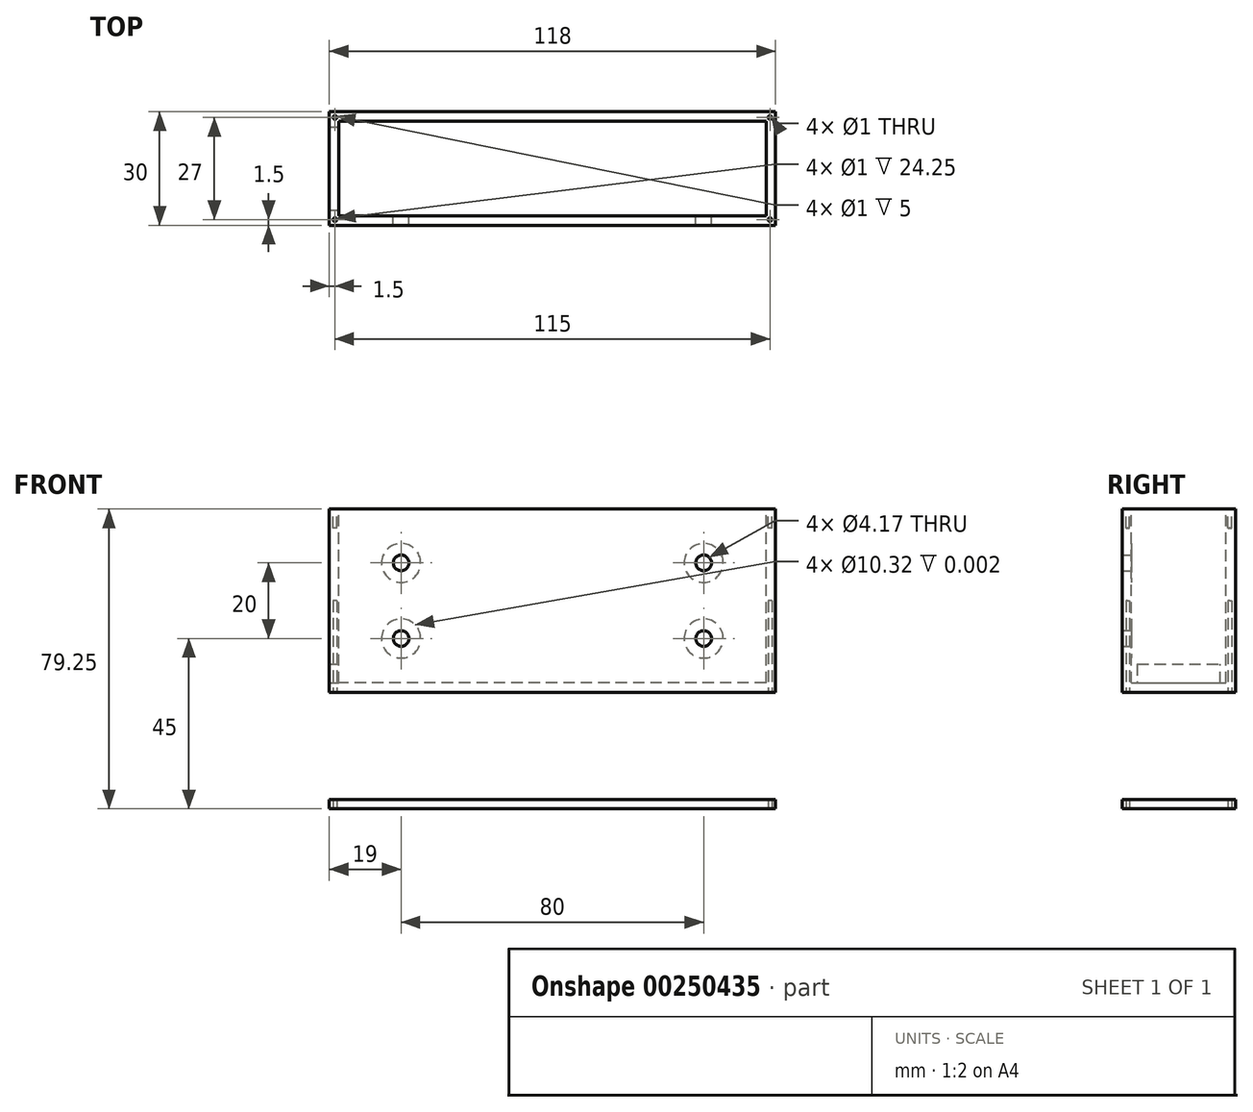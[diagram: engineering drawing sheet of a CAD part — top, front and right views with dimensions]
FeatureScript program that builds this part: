
annotation { "Feature Type Name" : "Feature", "Feature Type Description" : "" }
export const myFeature = defineFeature(function(context is Context, id is Id, definition is map)
    precondition{}
    {
        {
            var Q0;
            Q0=qCreatedBy(makeId("Front.planeOp"),FACE);
            var sketch = newSketch(context, id + "F0", { "sketchPlane" : qUnion([Q0])});
            skLineSegment(sketch, "E0.bottom", {"start": v(59, -24.25) * mm, "end": v(-59, -24.25) * mm});
            skLineSegment(sketch, "E0.top", {"start": v(59, 24.25) * mm, "end": v(-59, 24.25) * mm});
            skLineSegment(sketch, "E0.left", {"start": v(59, -24.25) * mm, "end": v(59, 24.25) * mm});
            skLineSegment(sketch, "E0.right", {"start": v(-59, -24.25) * mm, "end": v(-59, 24.25) * mm});
            skPoint(sketch, "E0.middle", {"position": v(0, 0) * mm});
            skSolve(sketch);
        }
        {
            var Q0;
            Q0 = qSketchRegion(id + "F0", true);
            extrude(context, id + "F1", {"entities" : qUnion([Q0]), "endBound" : BoundingType.SYMMETRIC, "depth" : 30 * mm});
        }
        {
            var Q0;
            Q0=makeQuery(id+"F1.opExtrude","SWEPT_FACE",FACE,{"disambiguationData":[OSD([sQuery(id+"F0.wireOp",EDGE,"E0.top")])]});
            shell(context, id + "F2", {"entities" : qUnion([Q0]), "thickness" : 2.5 * mm});
        }
        {
            var Q0;
            Q0=qCreatedBy(makeId("Right.planeOp"),FACE);
            var sketch = newSketch(context, id + "F3", { "sketchPlane" : qUnion([Q0])});
            skLineSegment(sketch, "E1", {"start": v(11, -16.75) * mm, "end": v(11, -21.75) * mm});
            skLineSegment(sketch, "E2", {"start": v(11, -21.75) * mm, "end": v(-11, -21.75) * mm});
            skLineSegment(sketch, "E3", {"start": v(-11, -21.75) * mm, "end": v(-11, -16.75) * mm});
            skLineSegment(sketch, "E4", {"start": v(11, -16.75) * mm, "end": v(-11, -16.75) * mm});
            skSolve(sketch);
        }
        {
            var Q0;
            Q0 = qSketchRegion(id + "F3", true);
            extrude(context, id + "F4", {"entities" : qUnion([Q0]), "operationType" : NewBodyOperationType.REMOVE, "oppositeDirection" : true, "depth" : 59.4 * mm});
        }
        {
            var Q0;
            Q0=qCreatedBy(makeId("Front.planeOp"),FACE);
            var sketch = newSketch(context, id + "F5", { "sketchPlane" : qUnion([Q0])});
            skCircle(sketch, "E5", {"center": v(40, -10) * mm, "radius": 2.08 * mm});
            skPoint(sketch, "E5.first.point", {"position": v(41.68, -8.77) * mm});
            skPoint(sketch, "E5.second.point", {"position": v(38.45, -11.4) * mm});
            skPoint(sketch, "E5.third.point", {"position": v(38.25, -8.87) * mm});
            skCircle(sketch, "E6", {"center": v(-40, -10) * mm, "radius": 2.08 * mm});
            skCircle(sketch, "E7", {"center": v(-40, 10) * mm, "radius": 2.08 * mm});
            skCircle(sketch, "E8", {"center": v(40, 10) * mm, "radius": 2.08 * mm});
            skSolve(sketch);
        }
        {
            var Q0;
            Q0 = qSketchRegion(id + "F5", true);
            extrude(context, id + "F6", {"entities" : qUnion([Q0]), "operationType" : NewBodyOperationType.REMOVE, "depth" : 25 * mm});
        }
        {
            var Q0;
            Q0=qCreatedBy(makeId("Top.planeOp"),FACE);
            cPlane(context, id + "F7", {"entities" : qUnion([Q0]), "cplaneType" : CPlaneType.OFFSET, "offset" : 55 * mm, "oppositeDirection" : true, "width" : 150 * mm, "height" : 150 * mm});
        }
        {
            var Q0;
            Q0=qCreatedBy(id+"F7.planeOp",FACE);
            var sketch = newSketch(context, id + "F8", { "sketchPlane" : qUnion([Q0])});
            skLineSegment(sketch, "E9.bottom", {"start": v(59, -15) * mm, "end": v(-59, -15) * mm});
            skLineSegment(sketch, "E9.top", {"start": v(59, 15) * mm, "end": v(-59, 15) * mm});
            skLineSegment(sketch, "E9.left", {"start": v(59, -15) * mm, "end": v(59, 15) * mm});
            skLineSegment(sketch, "E9.right", {"start": v(-59, -15) * mm, "end": v(-59, 15) * mm});
            skPoint(sketch, "E9.middle", {"position": v(0, 0) * mm});
            skSolve(sketch);
        }
        {
            var Q0;
            Q0 = qSketchRegion(id + "F8", true);
            extrude(context, id + "F9", {"entities" : qUnion([Q0]), "depth" : 2.5 * mm});
        }
        {
            var Q0;
            Q0=qCreatedBy(id+"F7.planeOp",FACE);
            var sketch = newSketch(context, id + "F10", { "sketchPlane" : qUnion([Q0])});
            skCircle(sketch, "E10", {"center": v(-57.5, 13.5) * mm, "radius": 0.5 * mm});
            skPoint(sketch, "E10.first.point", {"position": v(-57.94, 13.27) * mm});
            skPoint(sketch, "E10.second.point", {"position": v(-57.62, 13.01) * mm});
            skPoint(sketch, "E10.third.point", {"position": v(-57.16, 13.87) * mm});
            skCircle(sketch, "E11", {"center": v(-57.5, -13.5) * mm, "radius": 0.5 * mm});
            skCircle(sketch, "E12", {"center": v(57.5, -13.5) * mm, "radius": 0.5 * mm});
            skCircle(sketch, "E13", {"center": v(57.5, 13.5) * mm, "radius": 0.5 * mm});
            skSolve(sketch);
        }
        {
            var Q0;
            Q0 = qSketchRegion(id + "F10", true);
            extrude(context, id + "F11", {"entities" : qUnion([Q0]), "operationType" : NewBodyOperationType.REMOVE, "depth" : 55 * mm});
        }
        {
            var Q0;
            Q0=makeQuery(id+"F1.opExtrude","SWEPT_FACE",FACE,{"disambiguationData":[OSD([sQuery(id+"F0.wireOp",EDGE,"E0.top")])]});
            var sketch = newSketch(context, id + "F12", { "sketchPlane" : qUnion([Q0])});
            skCircle(sketch, "E14", {"center": v(-57.5, 13.5) * mm, "radius": 0.5 * mm});
            skPoint(sketch, "E14.first.point", {"position": v(-58, 13.5) * mm});
            skPoint(sketch, "E14.second.point", {"position": v(-57.8, 13.1) * mm});
            skPoint(sketch, "E14.third.point", {"position": v(-57.46, 14) * mm});
            skCircle(sketch, "E15", {"center": v(-57.5, -13.5) * mm, "radius": 0.5 * mm});
            skCircle(sketch, "E16", {"center": v(57.5, -13.5) * mm, "radius": 0.5 * mm});
            skCircle(sketch, "E17", {"center": v(57.5, 13.5) * mm, "radius": 0.5 * mm});
            skSolve(sketch);
        }
        {
            var Q0;
            Q0 = qSketchRegion(id + "F12", true);
            extrude(context, id + "F13", {"entities" : qUnion([Q0]), "operationType" : NewBodyOperationType.REMOVE, "oppositeDirection" : true, "depth" : 5 * mm});
        }
        {
            var Q0;
            {var subQ0=sQuery(id+"F0.wireOp",EDGE,"E0.right");var subQ1=sQuery(id+"F0.wireOp",EDGE,"E0.left");var subQ2=sQuery(id+"F0.wireOp",EDGE,"E0.top");var subQ3=sQuery(id+"F0.wireOp",EDGE,"E0.bottom");Q0=makeQuery(id+"F2.opShell","OFFSET_FACE",FACE,{"disambiguationData":[OSD([subQ3,subQ2,subQ1,subQ0]),TDD([makeQuery(id+"F1.opExtrude","CAP_FACE",FACE,{"disambiguationData":[OSD([subQ3,subQ2,subQ1,subQ0])],"isStart":false})])]});}
            var sketch = newSketch(context, id + "F14", { "sketchPlane" : qUnion([Q0])});
            skCircle(sketch, "E18", {"center": v(40, -10) * mm, "radius": 5.16 * mm});
            skCircle(sketch, "E19", {"center": v(40, 10) * mm, "radius": 5.16 * mm});
            skCircle(sketch, "E20", {"center": v(-40, 10) * mm, "radius": 5.16 * mm});
            skCircle(sketch, "E21", {"center": v(-40, -10) * mm, "radius": 5.16 * mm});
            skSolve(sketch);
        }
        {
            var Q0;
            Q0 = qSketchRegion(id + "F14", true);
            extrude(context, id + "F15", {"entities" : qUnion([Q0]), "operationType" : NewBodyOperationType.REMOVE, "oppositeDirection" : true, "depth" : 1 / 406.4 * mm});
        }
    });
